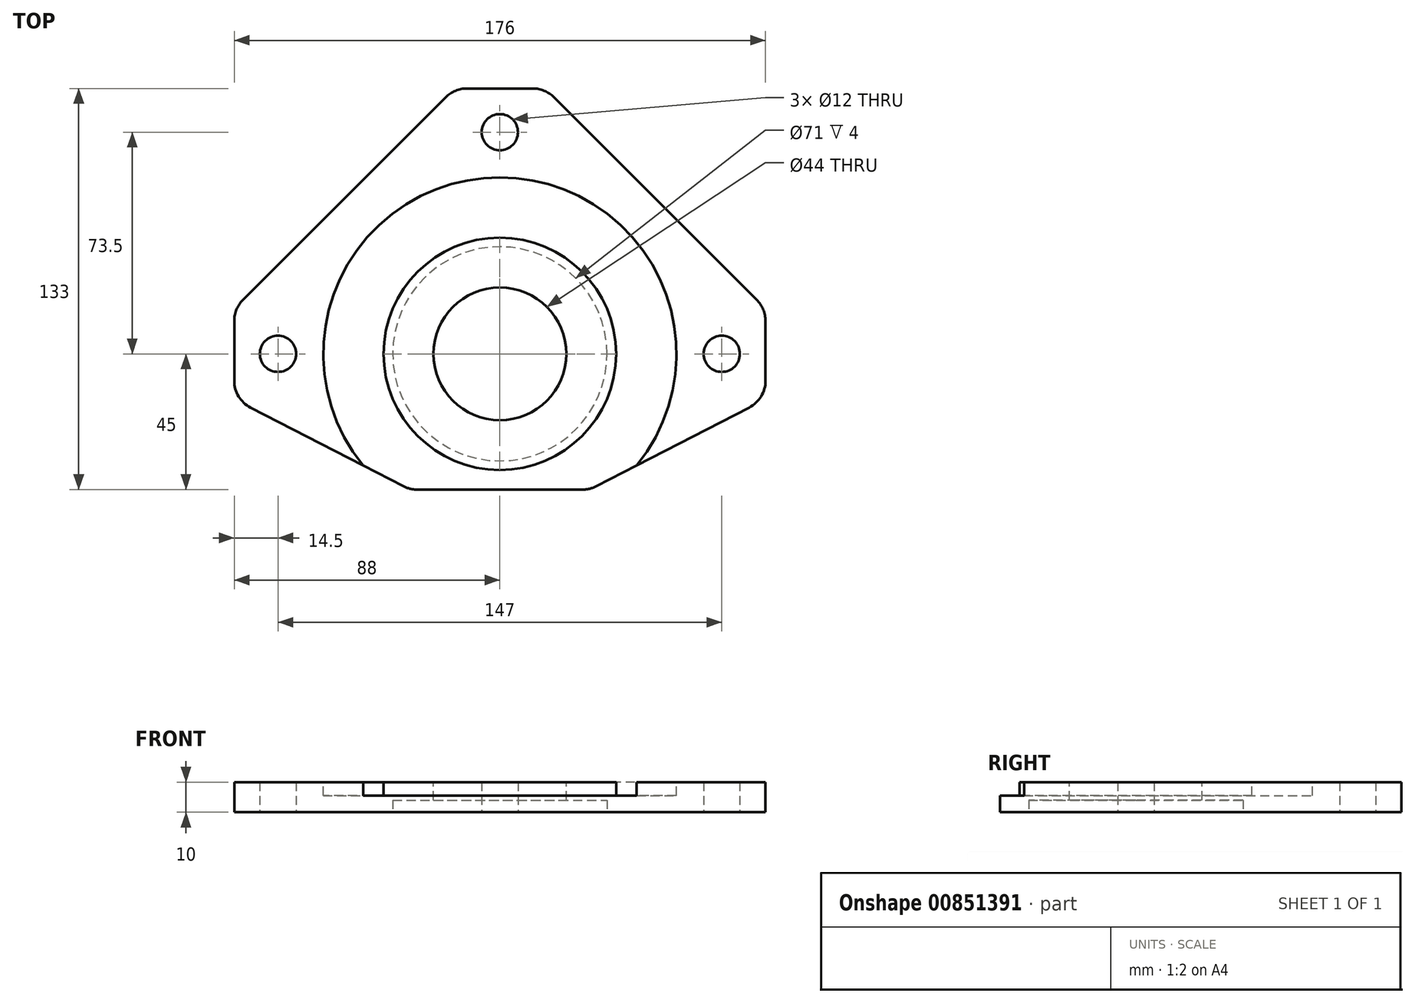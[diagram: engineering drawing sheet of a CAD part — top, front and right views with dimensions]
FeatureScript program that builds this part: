
annotation { "Feature Type Name" : "Feature", "Feature Type Description" : "" }
export const myFeature = defineFeature(function(context is Context, id is Id, definition is map)
    precondition{}
    {
        {
            var Q0;
            Q0=qCreatedBy(makeId("Top.planeOp"),FACE);
            var sketch = newSketch(context, id + "F0", { "sketchPlane" : qUnion([Q0])});
            skLineSegment(sketch, "E0", {"start": v(-116.46, 0) * mm, "end": v(116.44, 0) * mm, "construction": true});
            skLineSegment(sketch, "E1", {"start": v(0, 95.3) * mm, "end": v(0, -88.43) * mm, "construction": true});
            skLineSegment(sketch, "E2", {"start": v(-88, 10.86) * mm, "end": v(-88, -8.9) * mm});
            skLineSegment(sketch, "E3.1.0", {"start": v(10.86, 88) * mm, "end": v(-10.86, 88) * mm});
            skLineSegment(sketch, "E3.2.0", {"start": v(88, -8.9) * mm, "end": v(88, 10.86) * mm});
            skPoint(sketch, "E3.center", {"position": v(0, 0) * mm});
            skLineSegment(sketch, "E3.anchor1", {"start": v(0, 0) * mm, "end": v(-88, -15) * mm, "construction": true});
            skLineSegment(sketch, "E3.anchor2", {"start": v(0, 0) * mm, "end": v(88, 15) * mm, "construction": true});
            skLineSegment(sketch, "E4", {"start": v(-17.93, 85.07) * mm, "end": v(-85.07, 17.93) * mm});
            skLineSegment(sketch, "E5", {"start": v(17.93, 85.07) * mm, "end": v(85.07, 17.93) * mm});
            skLineSegment(sketch, "E6", {"start": v(82.58, -17.8) * mm, "end": v(31.97, -43.89) * mm});
            skLineSegment(sketch, "E7", {"start": v(27.39, -45) * mm, "end": v(0, -45) * mm});
            skLineSegment(sketch, "E8.MirrorCS", {"start": v(-27.39, -45) * mm, "end": v(0, -45) * mm});
            skLineSegment(sketch, "E9.MirrorCS", {"start": v(-82.58, -17.8) * mm, "end": v(-31.97, -43.89) * mm});
            skPoint(sketch, "E10.visualSharp", {"position": v(-15, 88) * mm});
            skArc(sketch, "E10.filletArc", {"start": v(-10.86, 88) * mm, "mid": v(-14.68, 87.24) * mm, "end": v(-17.93, 85.07) * mm});
            skPoint(sketch, "E11.visualSharp", {"position": v(15, 88) * mm});
            skArc(sketch, "E11.filletArc", {"start": v(17.93, 85.07) * mm, "mid": v(14.68, 87.24) * mm, "end": v(10.86, 88) * mm});
            skPoint(sketch, "E12.visualSharp", {"position": v(88, 15) * mm});
            skArc(sketch, "E12.filletArc", {"start": v(88, 10.86) * mm, "mid": v(87.24, 14.68) * mm, "end": v(85.07, 17.93) * mm});
            skPoint(sketch, "E13.visualSharp", {"position": v(88, -15) * mm});
            skArc(sketch, "E13.filletArc", {"start": v(82.58, -17.8) * mm, "mid": v(86.54, -14.1) * mm, "end": v(88, -8.9) * mm});
            skPoint(sketch, "E14.visualSharp", {"position": v(29.82, -45) * mm});
            skArc(sketch, "E14.filletArc", {"start": v(27.39, -45) * mm, "mid": v(29.75, -44.72) * mm, "end": v(31.97, -43.89) * mm});
            skPoint(sketch, "E15.visualSharp", {"position": v(-29.82, -45) * mm});
            skArc(sketch, "E15.filletArc", {"start": v(-31.97, -43.89) * mm, "mid": v(-29.75, -44.72) * mm, "end": v(-27.39, -45) * mm});
            skPoint(sketch, "E16.visualSharp", {"position": v(-88, -15) * mm});
            skArc(sketch, "E16.filletArc", {"start": v(-88, -8.9) * mm, "mid": v(-86.54, -14.1) * mm, "end": v(-82.58, -17.8) * mm});
            skPoint(sketch, "E17.visualSharp", {"position": v(-88, 15) * mm});
            skArc(sketch, "E17.filletArc", {"start": v(-85.07, 17.93) * mm, "mid": v(-87.24, 14.68) * mm, "end": v(-88, 10.86) * mm});
            skCircle(sketch, "E18", {"center": v(-73.5, 0) * mm, "radius": 6 * mm});
            skCircle(sketch, "E19.1.0", {"center": v(0, 73.5) * mm, "radius": 6 * mm});
            skCircle(sketch, "E19.2.0", {"center": v(73.5, 0) * mm, "radius": 6 * mm});
            skLineSegment(sketch, "E19.anchor1", {"start": v(0, 0) * mm, "end": v(-73.5, 0) * mm, "construction": true});
            skLineSegment(sketch, "E19.anchor2", {"start": v(0, 0) * mm, "end": v(73.5, 0) * mm, "construction": true});
            skSolve(sketch);
        }
        {
            var Q0;
            Q0 = qSketchRegion(id + "F0", true);
            extrude(context, id + "F1", {"entities" : qUnion([Q0]), "depth" : 10 * mm, "offsetDistance" : 25 * mm});
        }
        {
            var Q0;
            Q0=makeQuery(id+"F1.opExtrude","CAP_FACE",FACE,{"disambiguationData":[OSD([sQuery(id+"F0.wireOp",EDGE,"E2"),sQuery(id+"F0.wireOp",EDGE,"E3.1.0"),sQuery(id+"F0.wireOp",EDGE,"E3.2.0"),sQuery(id+"F0.wireOp",EDGE,"E4"),sQuery(id+"F0.wireOp",EDGE,"E5"),sQuery(id+"F0.wireOp",EDGE,"E6"),sQuery(id+"F0.wireOp",EDGE,"E7"),sQuery(id+"F0.wireOp",EDGE,"E8.MirrorCS"),sQuery(id+"F0.wireOp",EDGE,"E9.MirrorCS"),sQuery(id+"F0.wireOp",EDGE,"E10.filletArc"),sQuery(id+"F0.wireOp",EDGE,"E11.filletArc"),sQuery(id+"F0.wireOp",EDGE,"E12.filletArc"),sQuery(id+"F0.wireOp",EDGE,"E13.filletArc"),sQuery(id+"F0.wireOp",EDGE,"E14.filletArc"),sQuery(id+"F0.wireOp",EDGE,"E15.filletArc"),sQuery(id+"F0.wireOp",EDGE,"E16.filletArc"),sQuery(id+"F0.wireOp",EDGE,"E17.filletArc")])],"isStart":true});
            var sketch = newSketch(context, id + "F2", { "sketchPlane" : qUnion([Q0])});
            skCircle(sketch, "E20", {"center": v(0, 0) * mm, "radius": 35.5 * mm});
            skSolve(sketch);
        }
        {
            var Q0;
            Q0 = qSketchRegion(id + "F2", true);
            extrude(context, id + "F3", {"entities" : qUnion([Q0]), "operationType" : NewBodyOperationType.REMOVE, "oppositeDirection" : true, "depth" : 4 * mm, "offsetDistance" : 25 * mm});
        }
        {
            var Q0;
            Q0=makeQuery(id+"F1.opExtrude","CAP_FACE",FACE,{"disambiguationData":[OSD([sQuery(id+"F0.wireOp",EDGE,"E2"),sQuery(id+"F0.wireOp",EDGE,"E3.1.0"),sQuery(id+"F0.wireOp",EDGE,"E3.2.0"),sQuery(id+"F0.wireOp",EDGE,"E4"),sQuery(id+"F0.wireOp",EDGE,"E5"),sQuery(id+"F0.wireOp",EDGE,"E6"),sQuery(id+"F0.wireOp",EDGE,"E7"),sQuery(id+"F0.wireOp",EDGE,"E8.MirrorCS"),sQuery(id+"F0.wireOp",EDGE,"E9.MirrorCS"),sQuery(id+"F0.wireOp",EDGE,"E10.filletArc"),sQuery(id+"F0.wireOp",EDGE,"E11.filletArc"),sQuery(id+"F0.wireOp",EDGE,"E12.filletArc"),sQuery(id+"F0.wireOp",EDGE,"E13.filletArc"),sQuery(id+"F0.wireOp",EDGE,"E14.filletArc"),sQuery(id+"F0.wireOp",EDGE,"E15.filletArc"),sQuery(id+"F0.wireOp",EDGE,"E16.filletArc"),sQuery(id+"F0.wireOp",EDGE,"E17.filletArc")])],"isStart":false});
            var sketch = newSketch(context, id + "F4", { "sketchPlane" : qUnion([Q0])});
            skCircle(sketch, "E21", {"center": v(0, 0) * mm, "radius": 38.5 * mm});
            skCircle(sketch, "E22", {"center": v(0, 0) * mm, "radius": 58.5 * mm});
            skSolve(sketch);
        }
        {
            var Q0;
            Q0 = qSketchRegion(id + "F4", true);
            extrude(context, id + "F5", {"entities" : qUnion([Q0]), "operationType" : NewBodyOperationType.REMOVE, "oppositeDirection" : true, "depth" : 4.5 * mm, "offsetDistance" : 25 * mm});
        }
        {
            var Q0;
            Q0=makeQuery(id+"F5.boolean.opBoolean","SPLIT",FACE,{"disambiguationData":[TD([makeQuery(id+"F5.opExtrude","SWEPT_FACE",FACE,{"disambiguationData":[OSD([sQuery(id+"F4.wireOp",EDGE,"E21")])]})])],"derivedFrom":makeQuery(id+"F1.opExtrude","CAP_FACE",FACE,{"disambiguationData":[OSD([sQuery(id+"F0.wireOp",EDGE,"E2"),sQuery(id+"F0.wireOp",EDGE,"E3.1.0"),sQuery(id+"F0.wireOp",EDGE,"E3.2.0"),sQuery(id+"F0.wireOp",EDGE,"E4"),sQuery(id+"F0.wireOp",EDGE,"E5"),sQuery(id+"F0.wireOp",EDGE,"E6"),sQuery(id+"F0.wireOp",EDGE,"E7"),sQuery(id+"F0.wireOp",EDGE,"E8.MirrorCS"),sQuery(id+"F0.wireOp",EDGE,"E9.MirrorCS"),sQuery(id+"F0.wireOp",EDGE,"E10.filletArc"),sQuery(id+"F0.wireOp",EDGE,"E11.filletArc"),sQuery(id+"F0.wireOp",EDGE,"E12.filletArc"),sQuery(id+"F0.wireOp",EDGE,"E13.filletArc"),sQuery(id+"F0.wireOp",EDGE,"E14.filletArc"),sQuery(id+"F0.wireOp",EDGE,"E15.filletArc"),sQuery(id+"F0.wireOp",EDGE,"E16.filletArc"),sQuery(id+"F0.wireOp",EDGE,"E17.filletArc")])],"isStart":false})});
            var sketch = newSketch(context, id + "F6", { "sketchPlane" : qUnion([Q0])});
            skCircle(sketch, "E23", {"center": v(0, 0) * mm, "radius": 22 * mm});
            skSolve(sketch);
        }
        {
            var Q0;
            Q0 = qSketchRegion(id + "F6", true);
            extrude(context, id + "F7", {"entities" : qUnion([Q0]), "operationType" : NewBodyOperationType.REMOVE, "endBound" : BoundingType.THROUGH_ALL, "oppositeDirection" : true, "depth" : 25 * mm, "offsetDistance" : 25 * mm});
        }
    });
